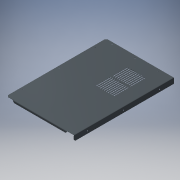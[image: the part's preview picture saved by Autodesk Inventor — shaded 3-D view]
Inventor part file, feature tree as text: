
AUTODESK INVENTOR PART (.ipt)
format: ipt  version: 2016 (Build 200138000, 138)  size: 408,064 bytes
history: native  units: mm
features: other x9, sheet_metal_op x7, sketch x7, reference x4, hole x2
ambient origin geometry x8: Origin, YZ Plane, XZ Plane, XY Plane, X Axis, Y Axis, Z Axis, Center Point
bodies: Solid1 (feature_tree)
feature tree (29):
  sheet_metal_op  "Face1"
  sheet_metal_op  "Flange1"
  sheet_metal_op  "Flange2"
  other  "Corner Chamfer1"
  hole  "Hole1"  [1 undecoded]
  hole  "Hole2"  [1 undecoded]
  other  "Corner Chamfer2"
  other  "Corner Chamfer3"
  sketch  "Sketch1"  dims[d0=1.0mm d1=1.0mm]
  reference  "Reference1"
  reference  "Reference2"
  reference  "Reference3"
  reference  "Reference4"
  other  "Plate1"
  sketch  "Sketch2"  dims[d2=0.5mm d3=2.0mm]
  other  "Plate2"
  sheet_metal_op  "Bend1"
  sheet_metal_op  "Corner1"
  sketch  "Sketch3"  dims[d4=1.0mm]
  other  "Plate3"
  sheet_metal_op  "Bend2"
  sheet_metal_op  "Corner2"
  sketch  "Sketch4"  dims[d5=22.0mm d6=90.0deg d7=1.0mm]
  sketch  "Sketch5"  dims[d8=4.0mm]
  sketch  "Sketch6"  dims[d9=1.0mm]
  sketch  "Sketch7"  dims[d10=1.0mm d11=1.0mm d12=0.5mm d13=2.0mm d14=1.0mm d15=8.0mm d16=90.0deg d17=1.0mm d18=4.0mm d19=1.0mm d20=1.0mm d21=24.0mm d22=26.0mm d23=2.0mm d24=0.0mm d25=60.0mm d26=1.5mm d27=60.0mm d28=60.0mm d29=20.0mm d31=70.0mm d32=100.0mm d34=8.0mm d37=1.0mm d38=0.0mm d39=6.0mm d40=6.0mm d41=45.0deg d42=10.0mm d43=10.0mm d47=55.0mm d48=150.0mm d49=150.0mm d50=3.0mm d51=6.0mm d52=4.0mm d53=2.0mm d54=90.0deg d55=1.0mm d56=20.594885mm d57=10.0mm d58=150.0mm d59=150.0mm d60=60.0mm d61=4.0mm d62=6.0mm d63=4.0mm d64=2.0mm d65=90.0deg d66=1.0mm d67=20.594885mm d68=6.0mm d69=6.0mm d70=45.0deg d71=90.0mm d72=90.0mm d73=18.0mm d74=6.0mm d75=45.0deg]
  other  "Cut1"
  other  "Cut2"
  other  "Definition1"
note: 2 required parameter values undecoded (feature->parameter linkage not recoverable at this tier; creation-order binding heuristic only, values carry confidence <= 0.55)
